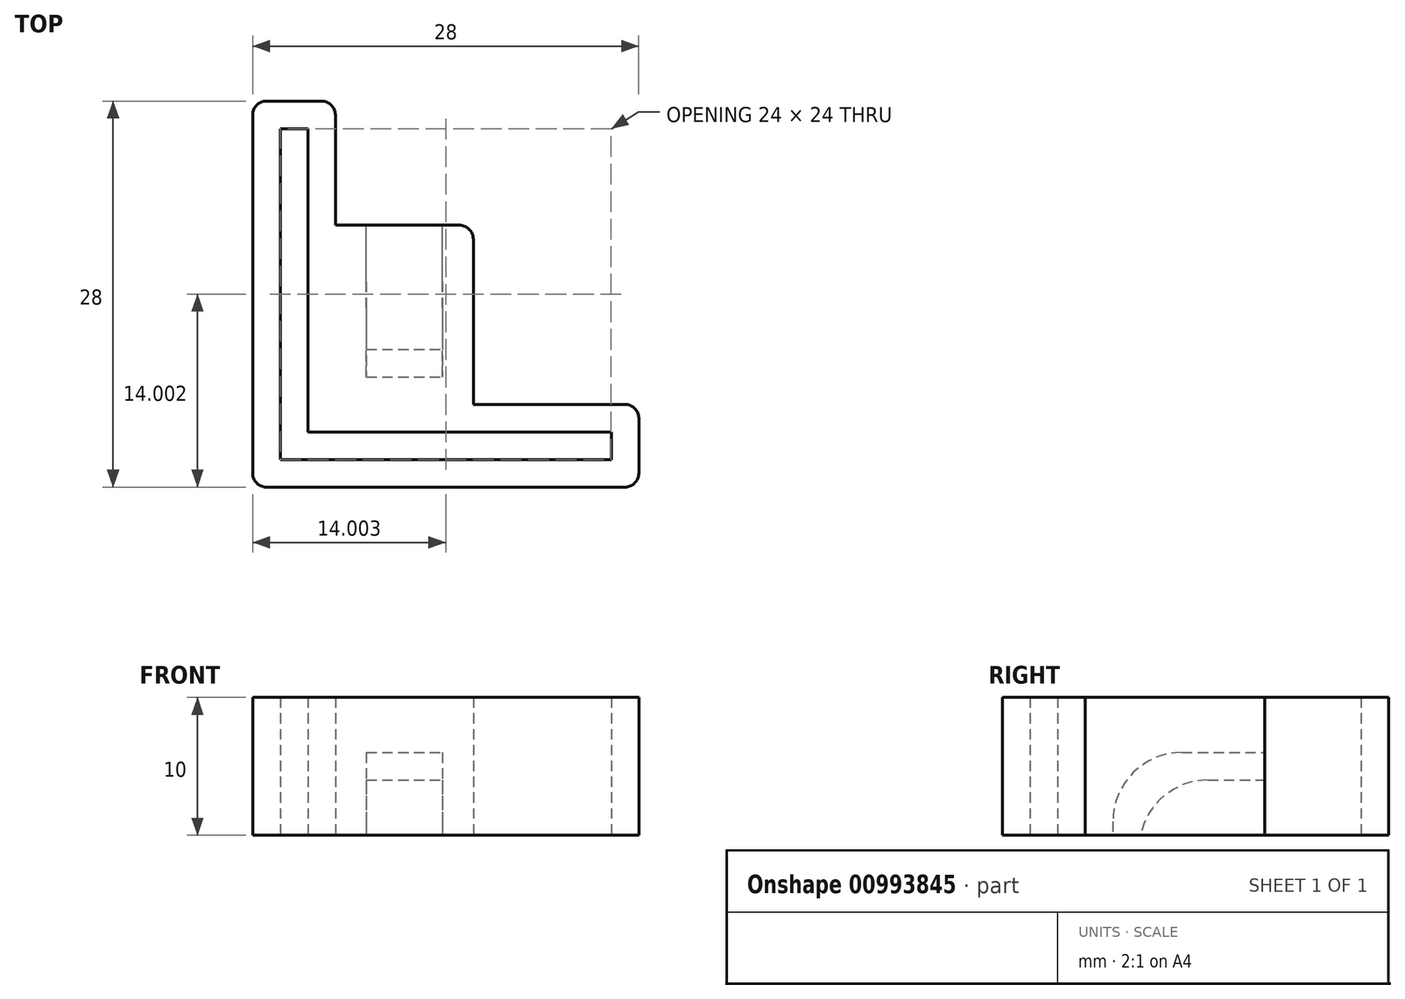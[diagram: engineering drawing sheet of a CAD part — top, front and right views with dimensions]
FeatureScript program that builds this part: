
annotation { "Feature Type Name" : "Feature", "Feature Type Description" : "" }
export const myFeature = defineFeature(function(context is Context, id is Id, definition is map)
    precondition{}
    {
        {
            var Q0;
            Q0=qCreatedBy(makeId("Top.planeOp"),FACE);
            var sketch = newSketch(context, id + "F0", { "sketchPlane" : qUnion([Q0])});
            skLineSegment(sketch, "E0", {"start": v(-10.78, -13.4) * mm, "end": v(-10.78, 10.6) * mm});
            skLineSegment(sketch, "E1", {"start": v(-10.78, 10.6) * mm, "end": v(13.22, 10.6) * mm});
            skLineSegment(sketch, "E2", {"start": v(13.22, 10.6) * mm, "end": v(13.22, 8.6) * mm});
            skLineSegment(sketch, "E3", {"start": v(13.22, 8.6) * mm, "end": v(-8.78, 8.6) * mm});
            skLineSegment(sketch, "E4", {"start": v(-8.78, 8.6) * mm, "end": v(-8.78, -13.4) * mm});
            skLineSegment(sketch, "E5", {"start": v(-8.78, -13.4) * mm, "end": v(-10.78, -13.4) * mm});
            skLineSegment(sketch, "E6", {"start": v(15.22, 6.6) * mm, "end": v(15.22, 12.6) * mm});
            skLineSegment(sketch, "E7", {"start": v(15.22, 12.6) * mm, "end": v(-12.78, 12.6) * mm});
            skLineSegment(sketch, "E8", {"start": v(-12.78, 12.6) * mm, "end": v(-12.78, -15.4) * mm});
            skLineSegment(sketch, "E9", {"start": v(-12.78, -15.4) * mm, "end": v(-6.78, -15.4) * mm});
            skLineSegment(sketch, "E10", {"start": v(-6.78, -15.4) * mm, "end": v(-6.78, 6.6) * mm});
            skLineSegment(sketch, "E11", {"start": v(-6.78, 6.6) * mm, "end": v(15.22, 6.6) * mm});
            skSolve(sketch);
        }
        {
            var Q0;
            Q0=makeQuery(id+"F0.imprint","IMPRINT",FACE,{"disambiguationData":[TD([[makeQuery(id+"F0.imprint","IMPRINT",EDGE,{"derivedFrom":sQuery(id+"F0.wireOp",EDGE,"E0")}),1.0]])]});
            extrude(context, id + "F1", {"entities" : qUnion([Q0]), "depth" : 10 * mm, "offsetDistance" : 25 * mm, "symmetric" : true});
        }
        {
            var Q0;
            Q0=makeQuery(id+"F1.opExtrude","SWEPT_FACE",FACE,{"disambiguationData":[OSD([sQuery(id+"F0.wireOp",EDGE,"E11")])]});
            var sketch = newSketch(context, id + "F2", { "sketchPlane" : qUnion([Q0])});
            skLineSegment(sketch, "E12.bottom", {"start": v(-6.78, 5) * mm, "end": v(3.22, 5) * mm});
            skLineSegment(sketch, "E12.top", {"start": v(-6.78, -5) * mm, "end": v(3.22, -5) * mm});
            skLineSegment(sketch, "E12.left", {"start": v(-6.78, 5) * mm, "end": v(-6.78, -5) * mm});
            skLineSegment(sketch, "E12.right", {"start": v(3.22, 5) * mm, "end": v(3.22, -5) * mm});
            skSolve(sketch);
        }
        {
            var Q0;
            Q0=makeQuery(id+"F2.imprint","IMPRINT",FACE,{"disambiguationData":[TD([[makeQuery(id+"F2.imprint","IMPRINT",EDGE,{"derivedFrom":sQuery(id+"F2.wireOp",EDGE,"E12.bottom")}),-1.0]])]});
            extrude(context, id + "F3", {"entities" : qUnion([Q0]), "operationType" : NewBodyOperationType.ADD, "depth" : 13 * mm, "offsetDistance" : 25 * mm});
        }
        {
            var Q0;
            Q0=makeQuery(id+"F3.opExtrude","CAP_EDGE",EDGE,{"disambiguationData":[OSD([sQuery(id+"F2.wireOp",EDGE,"E12.right")])],"isStart":true});
            var Q1;
            Q1=makeQuery(id+"F3.opExtrude","CAP_EDGE",EDGE,{"disambiguationData":[OSD([sQuery(id+"F2.wireOp",EDGE,"E12.top")])],"isStart":true});
            var Q2;
            Q2=makeQuery(id+"F3.opExtrude","CAP_EDGE",EDGE,{"disambiguationData":[OSD([sQuery(id+"F2.wireOp",EDGE,"E12.bottom")])],"isStart":true});
            var Q3;
            Q3=makeQuery(id+"F1.opExtrude","SWEPT_EDGE",EDGE,{"disambiguationData":[OSD([sQuery(id+"F0.wireOp",EDGE,"E7"),sQuery(id+"F0.wireOp",EDGE,"E8")])]});
            var Q4;
            Q4=makeQuery(id+"F1.opExtrude","SWEPT_EDGE",EDGE,{"disambiguationData":[OSD([sQuery(id+"F0.wireOp",EDGE,"E6"),sQuery(id+"F0.wireOp",EDGE,"E7")])]});
            var Q5;
            Q5=makeQuery(id+"F1.opExtrude","SWEPT_EDGE",EDGE,{"disambiguationData":[OSD([sQuery(id+"F0.wireOp",EDGE,"E6"),sQuery(id+"F0.wireOp",EDGE,"E11")])]});
            var Q6;
            Q6=makeQuery(id+"F1.opExtrude","SWEPT_EDGE",EDGE,{"disambiguationData":[OSD([sQuery(id+"F0.wireOp",EDGE,"E8"),sQuery(id+"F0.wireOp",EDGE,"E9")])]});
            var Q7;
            Q7=makeQuery(id+"F1.opExtrude","SWEPT_EDGE",EDGE,{"disambiguationData":[OSD([sQuery(id+"F0.wireOp",EDGE,"E9"),sQuery(id+"F0.wireOp",EDGE,"E10")])]});
            var Q8;
            Q8=makeQuery(id+"F3.opExtrude","CAP_EDGE",EDGE,{"disambiguationData":[OSD([sQuery(id+"F2.wireOp",EDGE,"E12.right")])],"isStart":false});
            var Q9;
            Q9=makeQuery(id+"F3.opExtrude","CAP_EDGE",EDGE,{"disambiguationData":[OSD([sQuery(id+"F2.wireOp",EDGE,"E12.left")])],"isStart":false});
            fillet(context, id + "F4", {"entities" : qUnion([Q0, Q1, Q2, Q3, Q4, Q5, Q6, Q7, Q8, Q9]), "radius" : 1 * mm, "defaultsChanged" : false, "vertexSettings" : [], "allowEdgeOverflow" : false});
        }
        {
            var Q0;
            Q0=makeQuery(id+"F3.opExtrude","CAP_FACE",FACE,{"disambiguationData":[OSD([sQuery(id+"F2.wireOp",EDGE,"E12.bottom"),sQuery(id+"F2.wireOp",EDGE,"E12.top"),sQuery(id+"F2.wireOp",EDGE,"E12.left"),sQuery(id+"F2.wireOp",EDGE,"E12.right")])],"isStart":false});
            var sketch = newSketch(context, id + "F5", { "sketchPlane" : qUnion([Q0])});
            skLineSegment(sketch, "E13.bottom", {"start": v(-4.53, 1) * mm, "end": v(0.97, 1) * mm});
            skLineSegment(sketch, "E13.top", {"start": v(-4.53, -1) * mm, "end": v(0.97, -1) * mm});
            skLineSegment(sketch, "E13.left", {"start": v(-4.53, 1) * mm, "end": v(-4.53, -1) * mm});
            skLineSegment(sketch, "E13.right", {"start": v(0.97, 1) * mm, "end": v(0.97, -1) * mm});
            skSolve(sketch);
        }
        {
            var Q0;
            Q0=makeQuery(id+"F3.boolean.opBoolean","MERGE",FACE,{"derivedFrom":[makeQuery(id+"F1.opExtrude","CAP_FACE",FACE,{"disambiguationData":[OSD([sQuery(id+"F0.wireOp",EDGE,"E0"),sQuery(id+"F0.wireOp",EDGE,"E1"),sQuery(id+"F0.wireOp",EDGE,"E2"),sQuery(id+"F0.wireOp",EDGE,"E3"),sQuery(id+"F0.wireOp",EDGE,"E4"),sQuery(id+"F0.wireOp",EDGE,"E5"),sQuery(id+"F0.wireOp",EDGE,"E6"),sQuery(id+"F0.wireOp",EDGE,"E7"),sQuery(id+"F0.wireOp",EDGE,"E8"),sQuery(id+"F0.wireOp",EDGE,"E9"),sQuery(id+"F0.wireOp",EDGE,"E10"),sQuery(id+"F0.wireOp",EDGE,"E11")])],"isStart":true}),makeQuery(id+"F3.opExtrude","SWEPT_FACE",FACE,{"disambiguationData":[OSD([sQuery(id+"F2.wireOp",EDGE,"E12.top")])]})]});
            var sketch = newSketch(context, id + "F6", { "sketchPlane" : qUnion([Q0])});
            skLineSegment(sketch, "E14.bottom", {"start": v(-4.53, -4.6) * mm, "end": v(0.97, -4.6) * mm});
            skLineSegment(sketch, "E14.top", {"start": v(-4.53, -2.6) * mm, "end": v(0.97, -2.6) * mm});
            skLineSegment(sketch, "E14.left", {"start": v(-4.53, -4.6) * mm, "end": v(-4.53, -2.6) * mm});
            skLineSegment(sketch, "E14.right", {"start": v(0.97, -4.6) * mm, "end": v(0.97, -2.6) * mm});
            skSolve(sketch);
        }
        {
            var Q0;
            Q0=makeQuery(id+"F5.imprint","IMPRINT",FACE,{"disambiguationData":[TD([[makeQuery(id+"F5.imprint","IMPRINT",EDGE,{"derivedFrom":sQuery(id+"F5.wireOp",EDGE,"E13.bottom")}),-1.0]])]});
            extrude(context, id + "F7", {"entities" : qUnion([Q0]), "operationType" : NewBodyOperationType.REMOVE, "oppositeDirection" : true, "depth" : 11 * mm, "offsetDistance" : 25 * mm});
        }
        {
            var Q0;
            Q0=makeQuery(id+"F6.imprint","IMPRINT",FACE,{"disambiguationData":[TD([[makeQuery(id+"F6.imprint","IMPRINT",EDGE,{"derivedFrom":sQuery(id+"F6.wireOp",EDGE,"E14.bottom")}),1.0]])]});
            var Q1;
            Q1=makeQuery(id+"F7.boolean.opBoolean","COPY",FACE,{"derivedFrom":makeQuery(id+"F7.opExtrude","SWEPT_FACE",FACE,{"disambiguationData":[OSD([sQuery(id+"F5.wireOp",EDGE,"E13.bottom")])]})});
            extrude(context, id + "F8", {"entities" : qUnion([Q0]), "operationType" : NewBodyOperationType.REMOVE, "endBound" : BoundingType.UP_TO_SURFACE, "oppositeDirection" : true, "depth" : 25 * mm, "endBoundEntityFace" : qUnion([Q1]), "offsetDistance" : 25 * mm});
        }
        {
            var Q0;
            Q0=makeQuery(id+"F7.boolean.opBoolean","COPY",EDGE,{"derivedFrom":makeQuery(id+"F7.opExtrude","CAP_EDGE",EDGE,{"disambiguationData":[OSD([sQuery(id+"F5.wireOp",EDGE,"E13.bottom")])],"isStart":false})});
            var Q1;
            Q1=makeQuery(id+"F8.boolean.opBoolean","INTERSECT",EDGE,{"derivedFrom":[makeQuery(id+"F7.boolean.opBoolean","COPY",FACE,{"derivedFrom":makeQuery(id+"F7.opExtrude","SWEPT_FACE",FACE,{"disambiguationData":[OSD([sQuery(id+"F5.wireOp",EDGE,"E13.top")])]})}),makeQuery(id+"F8.opExtrude","SWEPT_FACE",FACE,{"disambiguationData":[OSD([sQuery(id+"F6.wireOp",EDGE,"E14.top")])]})]});
            fillet(context, id + "F9", {"entities" : qUnion([Q0, Q1]), "tangentPropagation" : true, "radius" : 5 * mm, "defaultsChanged" : true, "vertexSettings" : [], "allowEdgeOverflow" : false});
        }
        {
            var Q0;
            Q0=makeQuery(id+"F1.opExtrude","SWEPT_BODY",BODY,{"disambiguationData":[OSD([sQuery(id+"F0.wireOp",EDGE,"E0"),sQuery(id+"F0.wireOp",EDGE,"E1"),sQuery(id+"F0.wireOp",EDGE,"E2"),sQuery(id+"F0.wireOp",EDGE,"E3"),sQuery(id+"F0.wireOp",EDGE,"E4"),sQuery(id+"F0.wireOp",EDGE,"E5"),sQuery(id+"F0.wireOp",EDGE,"E6"),sQuery(id+"F0.wireOp",EDGE,"E7"),sQuery(id+"F0.wireOp",EDGE,"E8"),sQuery(id+"F0.wireOp",EDGE,"E9"),sQuery(id+"F0.wireOp",EDGE,"E10"),sQuery(id+"F0.wireOp",EDGE,"E11")])]});
            transform(context, id + "F10", {"entities" : qUnion([Q0]), "transformType" : TransformType.TRANSLATION_3D, "dx" : 0 * mm, "dy" : -20 * mm, "dz" : 0 * mm, "makeCopy" : false});
        }
        {
            var Q0;
            Q0=makeQuery(id+"F1.opExtrude","SWEPT_BODY",BODY,{"disambiguationData":[OSD([sQuery(id+"F0.wireOp",EDGE,"E0"),sQuery(id+"F0.wireOp",EDGE,"E1"),sQuery(id+"F0.wireOp",EDGE,"E2"),sQuery(id+"F0.wireOp",EDGE,"E3"),sQuery(id+"F0.wireOp",EDGE,"E4"),sQuery(id+"F0.wireOp",EDGE,"E5"),sQuery(id+"F0.wireOp",EDGE,"E6"),sQuery(id+"F0.wireOp",EDGE,"E7"),sQuery(id+"F0.wireOp",EDGE,"E8"),sQuery(id+"F0.wireOp",EDGE,"E9"),sQuery(id+"F0.wireOp",EDGE,"E10"),sQuery(id+"F0.wireOp",EDGE,"E11")])]});
            var Q1;
            Q1=qCreatedBy(makeId("Front.planeOp"),FACE);
            mirror(context, id + "F11", {"entities" : qUnion([Q0]), "mirrorPlane" : qUnion([Q1])});
        }
        {
            var Q0;
            Q0=makeQuery(id+"F1.opExtrude","SWEPT_BODY",BODY,{"disambiguationData":[OSD([sQuery(id+"F0.wireOp",EDGE,"E0"),sQuery(id+"F0.wireOp",EDGE,"E1"),sQuery(id+"F0.wireOp",EDGE,"E2"),sQuery(id+"F0.wireOp",EDGE,"E3"),sQuery(id+"F0.wireOp",EDGE,"E4"),sQuery(id+"F0.wireOp",EDGE,"E5"),sQuery(id+"F0.wireOp",EDGE,"E6"),sQuery(id+"F0.wireOp",EDGE,"E7"),sQuery(id+"F0.wireOp",EDGE,"E8"),sQuery(id+"F0.wireOp",EDGE,"E9"),sQuery(id+"F0.wireOp",EDGE,"E10"),sQuery(id+"F0.wireOp",EDGE,"E11")])]});
            deleteBodies(context, id + "F12", {"entities" : qUnion([Q0])});
        }
    });
